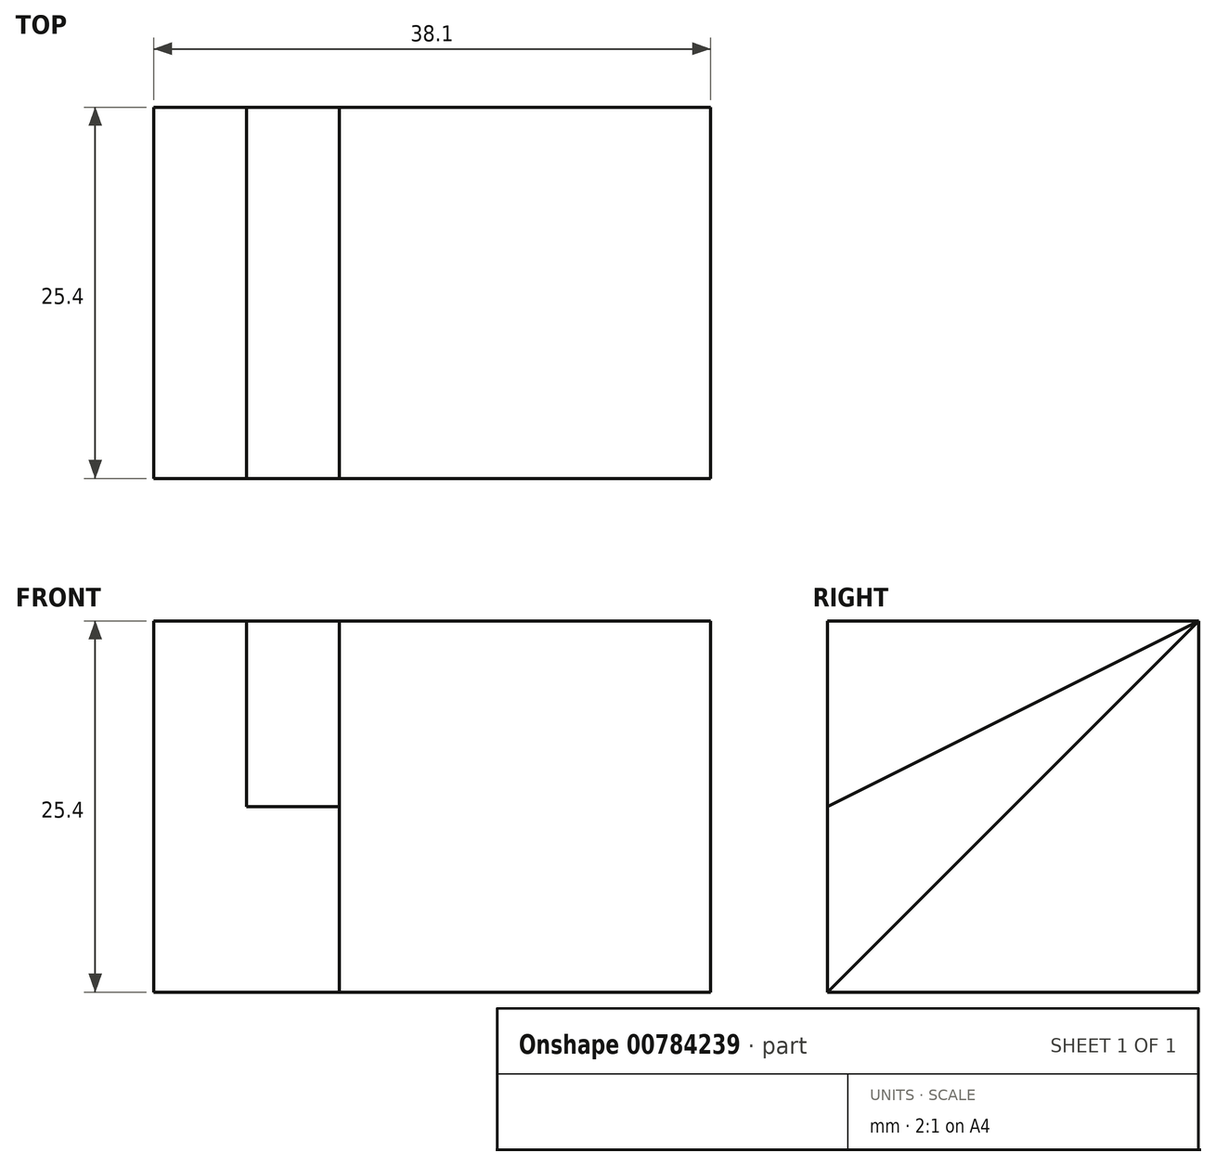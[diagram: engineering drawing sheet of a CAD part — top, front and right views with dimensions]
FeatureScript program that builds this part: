
annotation { "Feature Type Name" : "Feature", "Feature Type Description" : "" }
export const myFeature = defineFeature(function(context is Context, id is Id, definition is map)
    precondition{}
    {
        {
            var Q0;
            Q0=qCreatedBy(makeId("Front.planeOp"),FACE);
            var sketch = newSketch(context, id + "F0", { "sketchPlane" : qUnion([Q0])});
            skLineSegment(sketch, "E0", {"start": v(0, 0) * mm, "end": v(38.1, 0) * mm});
            skLineSegment(sketch, "E1", {"start": v(38.1, 0) * mm, "end": v(38.1, 25.4) * mm});
            skLineSegment(sketch, "E2", {"start": v(38.1, 25.4) * mm, "end": v(0, 25.4) * mm});
            skLineSegment(sketch, "E3", {"start": v(0, 25.4) * mm, "end": v(0, 0) * mm});
            skSolve(sketch);
        }
        {
            var Q0;
            Q0=makeQuery(id+"F0.imprint","IMPRINT",FACE,{"disambiguationData":[TD([[makeQuery(id+"F0.imprint","IMPRINT",EDGE,{"derivedFrom":sQuery(id+"F0.wireOp",EDGE,"E0")}),1.0]])]});
            extrude(context, id + "F1", {"entities" : qUnion([Q0]), "depth" : 25.4 * mm, "offsetDistance" : 25.4 * mm});
        }
        {
            var Q0;
            Q0=makeQuery(id+"F1.opExtrude","SWEPT_FACE",FACE,{"disambiguationData":[OSD([sQuery(id+"F0.wireOp",EDGE,"E1")])]});
            var sketch = newSketch(context, id + "F2", { "sketchPlane" : qUnion([Q0])});
            skLineSegment(sketch, "E4", {"start": v(-25.4, 0) * mm, "end": v(0, 25.4) * mm});
            skSolve(sketch);
        }
        {
            var Q0;
            Q0=makeQuery(id+"F2.imprint","IMPRINT",FACE,{"disambiguationData":[TD([[makeQuery(id+"F2.imprint","IMPRINT",EDGE,{"derivedFrom":sQuery(id+"F2.wireOp",EDGE,"E4")}),1.0]])]});
            extrude(context, id + "F3", {"entities" : qUnion([Q0]), "operationType" : NewBodyOperationType.REMOVE, "oppositeDirection" : true, "depth" : 25.4 * mm, "offsetDistance" : 25.4 * mm});
        }
        {
            var Q0;
            Q0=makeQuery(id+"F3.boolean.opBoolean","COPY",FACE,{"derivedFrom":makeQuery(id+"F3.opExtrude","CAP_FACE",FACE,{"disambiguationData":[OSD([sQuery(id+"F0.wireOp",EDGE,"E1"),sQuery(id+"F0.wireOp",EDGE,"E2"),sQuery(id+"F2.wireOp",EDGE,"E4")])],"isStart":false})});
            var sketch = newSketch(context, id + "F4", { "sketchPlane" : qUnion([Q0])});
            skLineSegment(sketch, "E5", {"start": v(0, 25.4) * mm, "end": v(-25.4, 12.7) * mm});
            skSolve(sketch);
        }
        {
            var Q0;
            Q0 = qSketchRegion(id + "F4", true);
            var Q1;
            {var subQ0=sQuery(id+"F4.wireOp",EDGE,"E5");Q1=makeQuery(id+"F4.imprint","IMPRINT",FACE,{"disambiguationData":[TD([[makeQuery(id+"F4.imprint","IMPRINT",EDGE,{"derivedFrom":subQ0}),-1.0]])]});}
            extrude(context, id + "F5", {"entities" : qUnion([Q0, Q1]), "operationType" : NewBodyOperationType.REMOVE, "oppositeDirection" : true, "depth" : 6.35 * mm, "offsetDistance" : 25.4 * mm});
        }
    });
